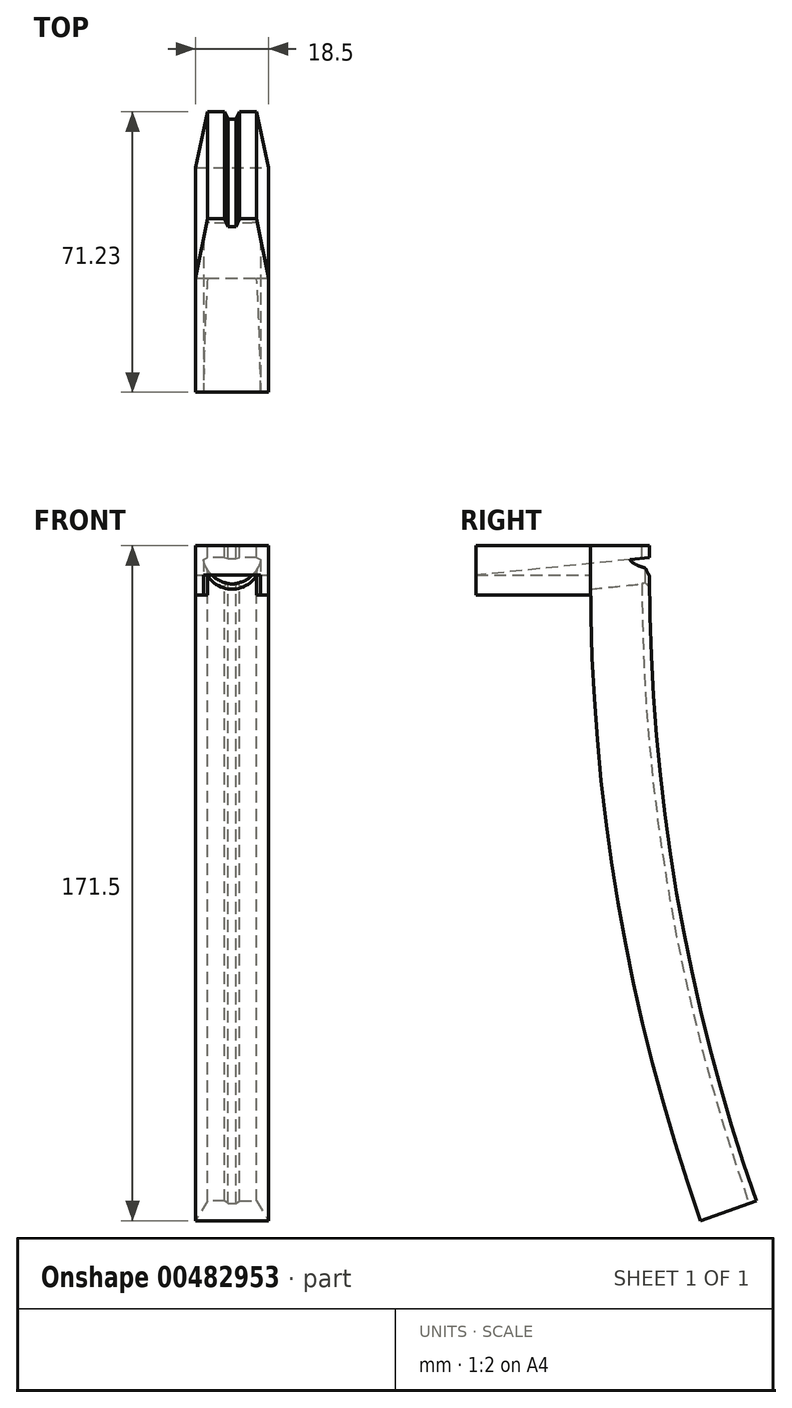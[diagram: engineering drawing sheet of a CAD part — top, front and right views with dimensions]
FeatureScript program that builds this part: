
annotation { "Feature Type Name" : "Feature", "Feature Type Description" : "" }
export const myFeature = defineFeature(function(context is Context, id is Id, definition is map)
    precondition{}
    {
        {
            var Q0;
            Q0=qCreatedBy(makeId("Top.planeOp"),FACE);
            var sketch = newSketch(context, id + "F0", { "sketchPlane" : qUnion([Q0])});
            skLineSegment(sketch, "E0", {"start": v(0, 0) * mm, "end": v(18.5, 0) * mm});
            skLineSegment(sketch, "E1", {"start": v(9.25, 0) * mm, "end": v(9.25, 15.08) * mm, "construction": true});
            skLineSegment(sketch, "E2", {"start": v(9.25, 15.08) * mm, "end": v(15.5, 15.08) * mm});
            skLineSegment(sketch, "E3", {"start": v(9.25, 15.08) * mm, "end": v(3, 15.08) * mm});
            skLineSegment(sketch, "E4", {"start": v(3, 15.08) * mm, "end": v(0, 0) * mm});
            skLineSegment(sketch, "E5", {"start": v(15.5, 15.08) * mm, "end": v(18.5, 0) * mm});
            skLineSegment(sketch, "E6.bottom", {"start": v(9.25, 15.08) * mm, "end": v(9.25, 15.08) * mm});
            skLineSegment(sketch, "E6.top", {"start": v(9.25, 13.08) * mm, "end": v(9.25, 13.08) * mm});
            skLineSegment(sketch, "E6.left", {"start": v(9.25, 15.08) * mm, "end": v(9.25, 13.08) * mm});
            skLineSegment(sketch, "E6.right", {"start": v(9.25, 15.08) * mm, "end": v(9.25, 13.08) * mm});
            skLineSegment(sketch, "E7", {"start": v(9.25, 13.08) * mm, "end": v(10.25, 13.08) * mm});
            skLineSegment(sketch, "E8", {"start": v(10.25, 13.08) * mm, "end": v(11.15, 15.08) * mm});
            skLineSegment(sketch, "E9.MirrorCS", {"start": v(8.25, 13.08) * mm, "end": v(7.35, 15.08) * mm});
            skLineSegment(sketch, "E10.MirrorCS", {"start": v(9.25, 13.08) * mm, "end": v(8.25, 13.08) * mm});
            skSolve(sketch);
        }
        {
            var Q0;
            Q0=qCreatedBy(makeId("Right.planeOp"),FACE);
            var sketch = newSketch(context, id + "F1", { "sketchPlane" : qUnion([Q0])});
            skLineSegment(sketch, "E11", {"start": v(0, 0) * mm, "end": v(0, -164) * mm, "construction": true});
            skLineSegment(sketch, "E12", {"start": v(0, -164) * mm, "end": v(28, -164) * mm, "construction": true});
            skArc(sketch, "E13", {"start": v(0, 0) * mm, "mid": v(7.05, -83.19) * mm, "end": v(28, -164) * mm});
            skLineSegment(sketch, "E14", {"start": v(0, 0) * mm, "end": v(0, 7.5) * mm});
            skSolve(sketch);
        }
        {
            var Q0;
            Q0=makeQuery(id+"F0.imprint","IMPRINT",FACE,{"disambiguationData":[TD([[makeQuery(id+"F0.imprint","IMPRINT",EDGE,{"derivedFrom":sQuery(id+"F0.wireOp",EDGE,"E0")}),1.0]])]});
            var Q1;
            Q1=sQuery(id+"F1.wireOp",EDGE,"E13");
            var Q2;
            Q2=sQuery(id+"F1.wireOp",EDGE,"E14");
            sweep(context, id + "F2", {"profiles" : qUnion([Q0]), "path" : qUnion([Q1, Q2])});
        }
        {
            var Q0;
            Q0=makeQuery(id+"F2.opSweep","SWEPT_FACE",FACE,{"disambiguationData":[OSD([sQuery(id+"F0.wireOp",EDGE,"E0"),sQuery(id+"F1.wireOp",EDGE,"E14")])]});
            extrude(context, id + "F3", {"entities" : qUnion([Q0]), "operationType" : NewBodyOperationType.ADD, "depth" : 29 * mm});
        }
        {
            var Q0;
            Q0=makeQuery(id+"F3.opExtrude","CAP_FACE",FACE,{"disambiguationData":[OSD([sQuery(id+"F0.wireOp",EDGE,"E0"),sQuery(id+"F1.wireOp",EDGE,"E14")])],"isStart":false});
            var sketch = newSketch(context, id + "F4", { "sketchPlane" : qUnion([Q0])});
            skLineSegment(sketch, "E15", {"start": v(0, 0) * mm, "end": v(2, 0) * mm, "construction": true});
            skLineSegment(sketch, "E16", {"start": v(9.25, 0) * mm, "end": v(9.25, -7.5) * mm, "construction": true});
            skLineSegment(sketch, "E17.MirrorCS", {"start": v(18.5, 0) * mm, "end": v(16.5, 0) * mm, "construction": true});
            skLineSegment(sketch, "E18", {"start": v(9.25, -7.5) * mm, "end": v(9.25, -6.5) * mm});
            skArc(sketch, "E19", {"start": v(2, 0) * mm, "mid": v(9.25, -6.5) * mm, "end": v(16.5, 0) * mm});
            skArc(sketch, "E20", {"start": v(16.5, 0) * mm, "mid": v(9.25, 8.09) * mm, "end": v(2, 0) * mm});
            skSolve(sketch);
        }
        {
            var Q0;
            Q0=qCreatedBy(makeId("Right.planeOp"),FACE);
            cPlane(context, id + "F5", {"entities" : qUnion([Q0]), "cplaneType" : CPlaneType.OFFSET, "offset" : 9.25 * mm, "width" : 150 * mm, "height" : 150 * mm});
        }
        {
            var Q0;
            Q0=qCreatedBy(id+"F5.planeOp",FACE);
            var sketch = newSketch(context, id + "F6", { "sketchPlane" : qUnion([Q0])});
            skLineSegment(sketch, "E21", {"start": v(-29.02, -4.5) * mm, "end": v(15.09, 0) * mm});
            skSolve(sketch);
        }
        {
            var Q0;
            {var subQ0=sQuery(id+"F4.wireOp",EDGE,"E19");var subQ1=makeQuery(id+"F4.imprint","INTERSECT",VERTEX,{"derivedFrom":[sQuery(id+"F4.wireOp",EDGE,"E18"),subQ0]});Q0=makeQuery(id+"F4.imprint","IMPRINT",FACE,{"disambiguationData":[TD([[makeQuery(id+"F4.imprint","IMPRINT",EDGE,{"disambiguationData":[TD([[subQ1,1.0]])],"derivedFrom":subQ0}),1.0]])]});}
            var Q1;
            Q1=sQuery(id+"F6.wireOp",EDGE,"E21");
            sweep(context, id + "F7", {"operationType" : NewBodyOperationType.REMOVE, "profiles" : qUnion([Q0]), "path" : qUnion([Q1])});
        }
        {
            var Q0;
            Q0=makeQuery(id+"F7.boolean.opBoolean","COPY",EDGE,{"derivedFrom":makeQuery(id+"F7.opSweep","CAP_EDGE",EDGE,{"disambiguationData":[OSD([sQuery(id+"F4.wireOp",EDGE,"E19"),sQuery(id+"F6.wireOp",VERTEX,"E21.start")])],"isStart":true})});
            chamfer(context, id + "F8", {"entities" : qUnion([Q0]), "width" : 1 * mm, "tangentPropagation" : true});
        }
        {
            var Q0;
            Q0=makeQuery(id+"F3.opExtrude","SWEPT_FACE",FACE,{"disambiguationData":[OSD([sQuery(id+"F0.wireOp",EDGE,"E0"),sQuery(id+"F1.wireOp",VERTEX,"E14.start")])]});
            extrude(context, id + "F9", {"entities" : qUnion([Q0]), "operationType" : NewBodyOperationType.ADD, "depth" : 5 * mm});
        }
    });
